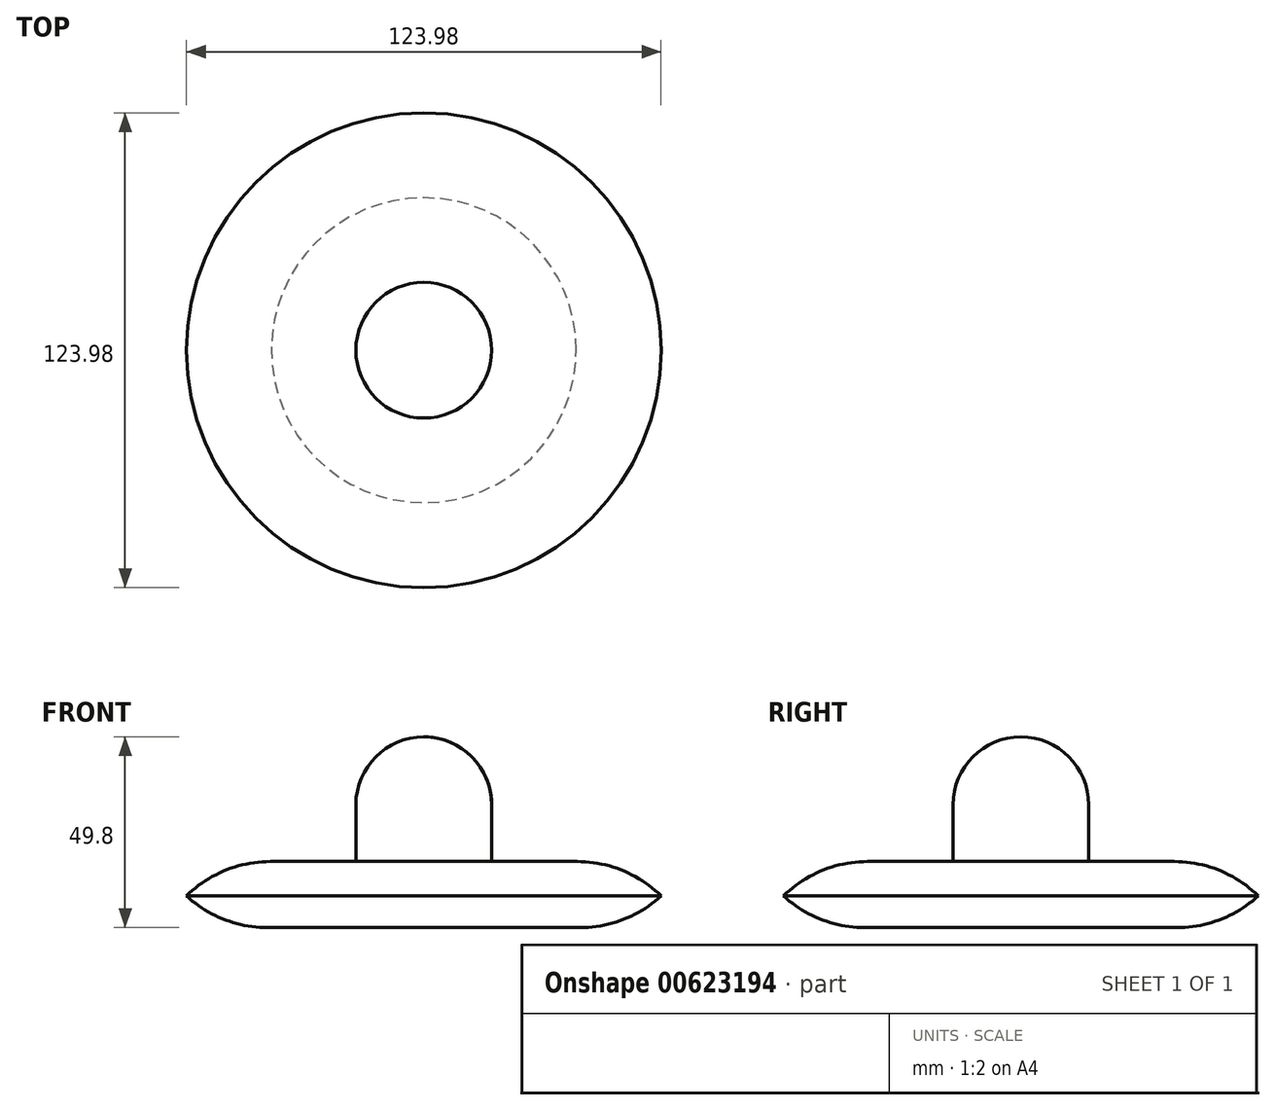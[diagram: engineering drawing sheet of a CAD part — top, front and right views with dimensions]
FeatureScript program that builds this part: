
annotation { "Feature Type Name" : "Feature", "Feature Type Description" : "" }
export const myFeature = defineFeature(function(context is Context, id is Id, definition is map)
    precondition{}
    {
        {
            var Q0;
            Q0=qCreatedBy(makeId("Front.planeOp"),FACE);
            var sketch = newSketch(context, id + "F0", { "sketchPlane" : qUnion([Q0])});
            skArc(sketch, "E0", {"start": v(17.73, 0) * mm, "mid": v(12.53, 12.53) * mm, "end": v(0, 17.73) * mm});
            skLineSegment(sketch, "E1", {"start": v(17.73, 0) * mm, "end": v(17.73, -14.83) * mm});
            skLineSegment(sketch, "E2", {"start": v(17.73, -14.83) * mm, "end": v(40.1, -14.83) * mm});
            skArc(sketch, "E3", {"start": v(62, -23.8) * mm, "mid": v(51.93, -17.16) * mm, "end": v(40.1, -14.83) * mm});
            skArc(sketch, "E4.MirrorCS", {"start": v(62, -23.8) * mm, "mid": v(51.71, -30.11) * mm, "end": v(39.8, -32.06) * mm});
            skLineSegment(sketch, "E5", {"start": v(39.8, -32.06) * mm, "end": v(0, -32.06) * mm});
            skPoint(sketch, "E6.endSnap0", {"position": v(51.04, -23.62) * mm});
            skPoint(sketch, "E6.end.orphan", {"position": v(-17.73, -23.62) * mm});
            skPoint(sketch, "E7.orphan", {"position": v(40.1, -23.44) * mm});
            skLineSegment(sketch, "E8", {"start": v(0, 17.73) * mm, "end": v(0, 0) * mm});
            skPoint(sketch, "E9.orphan", {"position": v(-17.73, 0) * mm});
            skLineSegment(sketch, "E10", {"start": v(0, 0) * mm, "end": v(0, -32.06) * mm});
            skSolve(sketch);
        }
        {
            var Q0;
            Q0=makeQuery(id+"F0.imprint","IMPRINT",FACE,{"disambiguationData":[TD([[makeQuery(id+"F0.imprint","IMPRINT",EDGE,{"derivedFrom":sQuery(id+"F0.wireOp",EDGE,"E0")}),1.0]])]});
            var Q1;
            Q1=sQuery(id+"F0.wireOp",EDGE,"E10");
            revolve(context, id + "F1", {"entities" : qUnion([Q0]), "axis" : qUnion([Q1]), "revolveType" : RevolveType.FULL});
        }
    });
